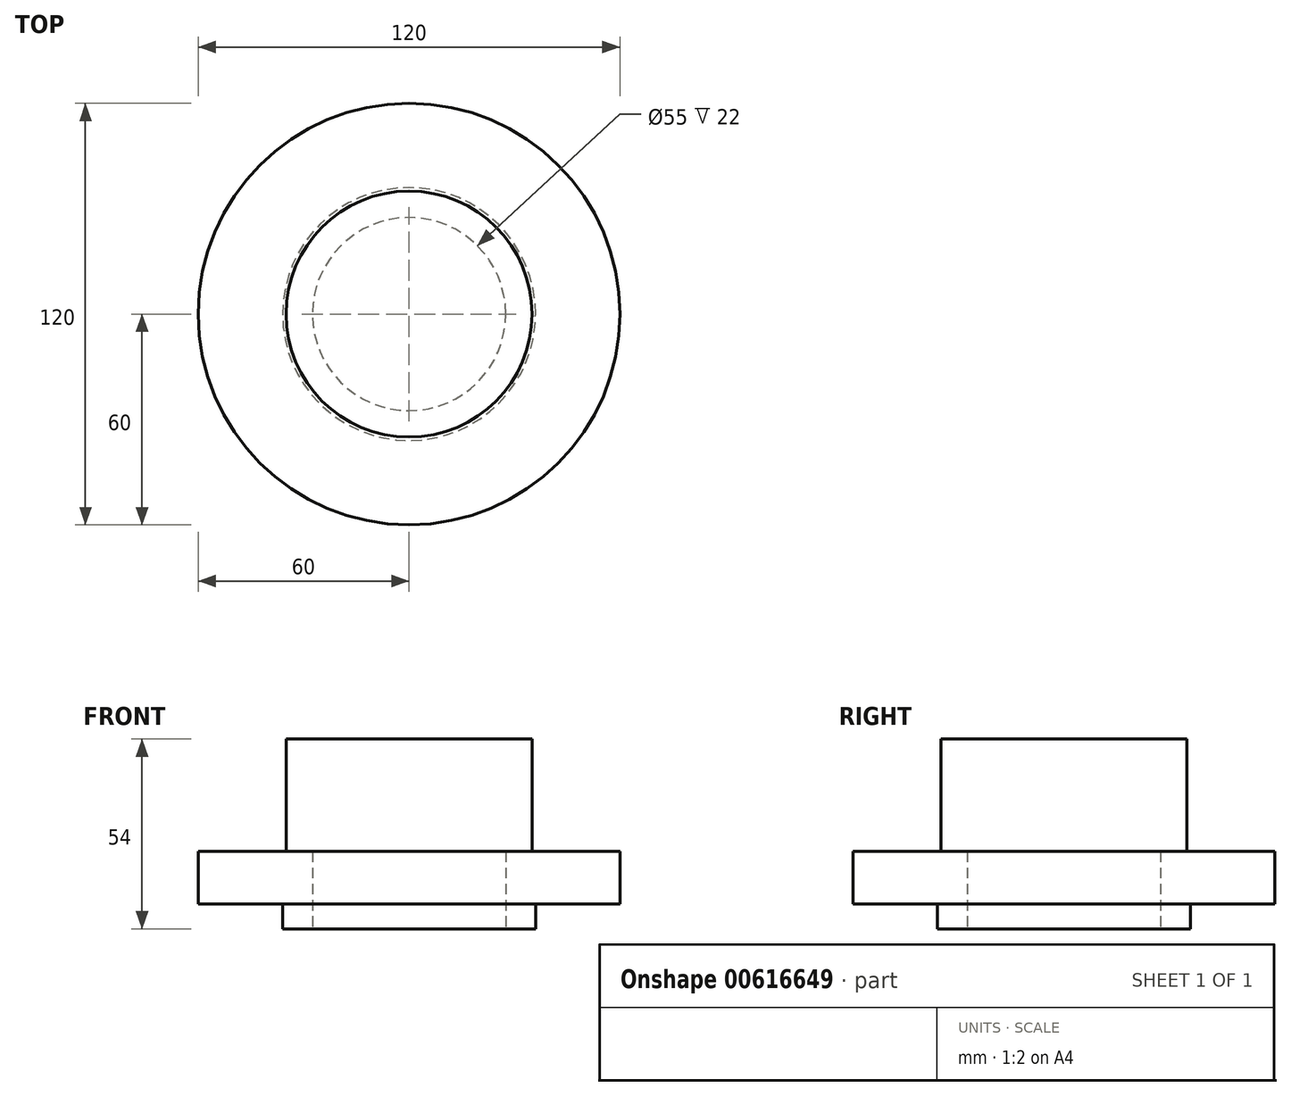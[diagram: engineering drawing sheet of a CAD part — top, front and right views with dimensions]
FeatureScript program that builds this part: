
annotation { "Feature Type Name" : "Feature", "Feature Type Description" : "" }
export const myFeature = defineFeature(function(context is Context, id is Id, definition is map)
    precondition{}
    {
        {
            var Q0;
            Q0=qCreatedBy(makeId("Top.planeOp"),FACE);
            var sketch = newSketch(context, id + "F0", { "sketchPlane" : qUnion([Q0])});
            skCircle(sketch, "E0", {"center": v(0, 0) * mm, "radius": 60 * mm});
            skSolve(sketch);
        }
        {
            var Q0;
            Q0=makeQuery(id+"F0.imprint","IMPRINT",FACE,{"disambiguationData":[TD([[makeQuery(id+"F0.imprint","IMPRINT",EDGE,{"derivedFrom":sQuery(id+"F0.wireOp",EDGE,"E0")}),1.0]])]});
            extrude(context, id + "F1", {"entities" : qUnion([Q0]), "oppositeDirection" : true, "depth" : 15 * mm, "offsetDistance" : 25 * mm});
        }
        {
            var Q0;
            Q0=makeQuery(id+"F1.opExtrude","CAP_FACE",FACE,{"disambiguationData":[OSD([sQuery(id+"F0.wireOp",EDGE,"E0")])],"isStart":true});
            var sketch = newSketch(context, id + "F2", { "sketchPlane" : qUnion([Q0])});
            skCircle(sketch, "E1", {"center": v(0, 0) * mm, "radius": 35 * mm});
            skSolve(sketch);
        }
        {
            var Q0;
            Q0=makeQuery(id+"F2.imprint","IMPRINT",FACE,{"disambiguationData":[TD([[makeQuery(id+"F2.imprint","IMPRINT",EDGE,{"derivedFrom":sQuery(id+"F2.wireOp",EDGE,"E1")}),1.0]])]});
            extrude(context, id + "F3", {"entities" : qUnion([Q0]), "operationType" : NewBodyOperationType.ADD, "depth" : 32 * mm, "offsetDistance" : 25 * mm});
        }
        {
            var Q0;
            Q0=makeQuery(id+"F1.opExtrude","CAP_FACE",FACE,{"disambiguationData":[OSD([sQuery(id+"F0.wireOp",EDGE,"E0")])],"isStart":false});
            var sketch = newSketch(context, id + "F4", { "sketchPlane" : qUnion([Q0])});
            skCircle(sketch, "E2", {"center": v(0, 0) * mm, "radius": 36 * mm});
            skSolve(sketch);
        }
        {
            var Q0;
            Q0=makeQuery(id+"F4.imprint","IMPRINT",FACE,{"disambiguationData":[TD([[makeQuery(id+"F4.imprint","IMPRINT",EDGE,{"derivedFrom":sQuery(id+"F4.wireOp",EDGE,"E2")}),1.0]])]});
            extrude(context, id + "F5", {"entities" : qUnion([Q0]), "operationType" : NewBodyOperationType.ADD, "depth" : 7 * mm, "offsetDistance" : 25 * mm});
        }
        {
            var Q0;
            Q0=makeQuery(id+"F5.opExtrude","CAP_FACE",FACE,{"disambiguationData":[OSD([sQuery(id+"F4.wireOp",EDGE,"E2")])],"isStart":false});
            var sketch = newSketch(context, id + "F6", { "sketchPlane" : qUnion([Q0])});
            skCircle(sketch, "E3", {"center": v(0, 0) * mm, "radius": 27.5 * mm});
            skSolve(sketch);
        }
        {
            var Q0;
            Q0=makeQuery(id+"F6.imprint","IMPRINT",FACE,{"disambiguationData":[TD([[makeQuery(id+"F6.imprint","IMPRINT",EDGE,{"derivedFrom":sQuery(id+"F6.wireOp",EDGE,"E3")}),1.0]])]});
            extrude(context, id + "F7", {"entities" : qUnion([Q0]), "operationType" : NewBodyOperationType.REMOVE, "oppositeDirection" : true, "depth" : 22 * mm, "offsetDistance" : 25 * mm});
        }
    });
